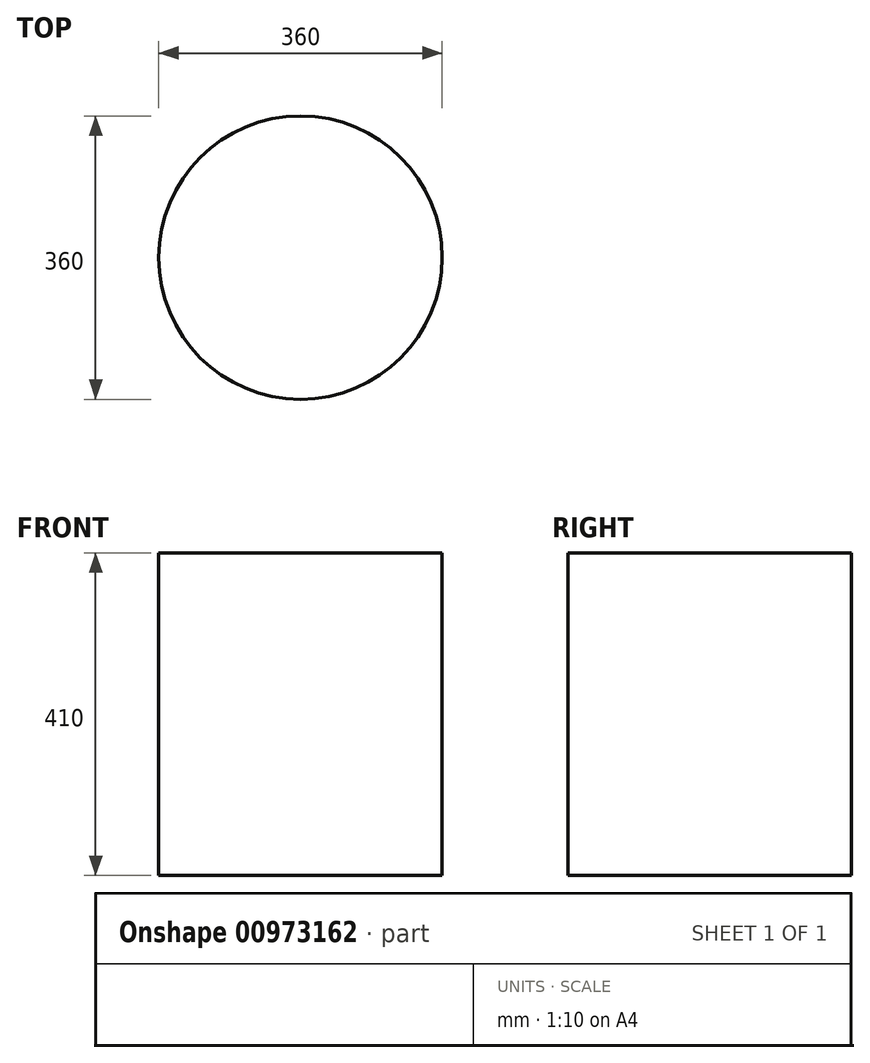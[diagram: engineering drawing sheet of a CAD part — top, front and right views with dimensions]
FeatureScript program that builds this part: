
annotation { "Feature Type Name" : "Feature", "Feature Type Description" : "" }
export const myFeature = defineFeature(function(context is Context, id is Id, definition is map)
    precondition{}
    {
        {
            var Q0;
            Q0=qCreatedBy(makeId("Top.planeOp"),FACE);
            var sketch = newSketch(context, id + "F0", { "sketchPlane" : qUnion([Q0])});
            skCircle(sketch, "E0", {"center": v(0, 0) * mm, "radius": 180 * mm});
            skSolve(sketch);
        }
        {
            var Q0;
            Q0=makeQuery(id+"F0.imprint","IMPRINT",FACE,{"disambiguationData":[TD([[makeQuery(id+"F0.imprint","IMPRINT",EDGE,{"derivedFrom":sQuery(id+"F0.wireOp",EDGE,"E0")}),1.0]])]});
            extrude(context, id + "F1", {"entities" : qUnion([Q0]), "depth" : 410 * mm, "offsetDistance" : 25 * mm});
        }
    });
